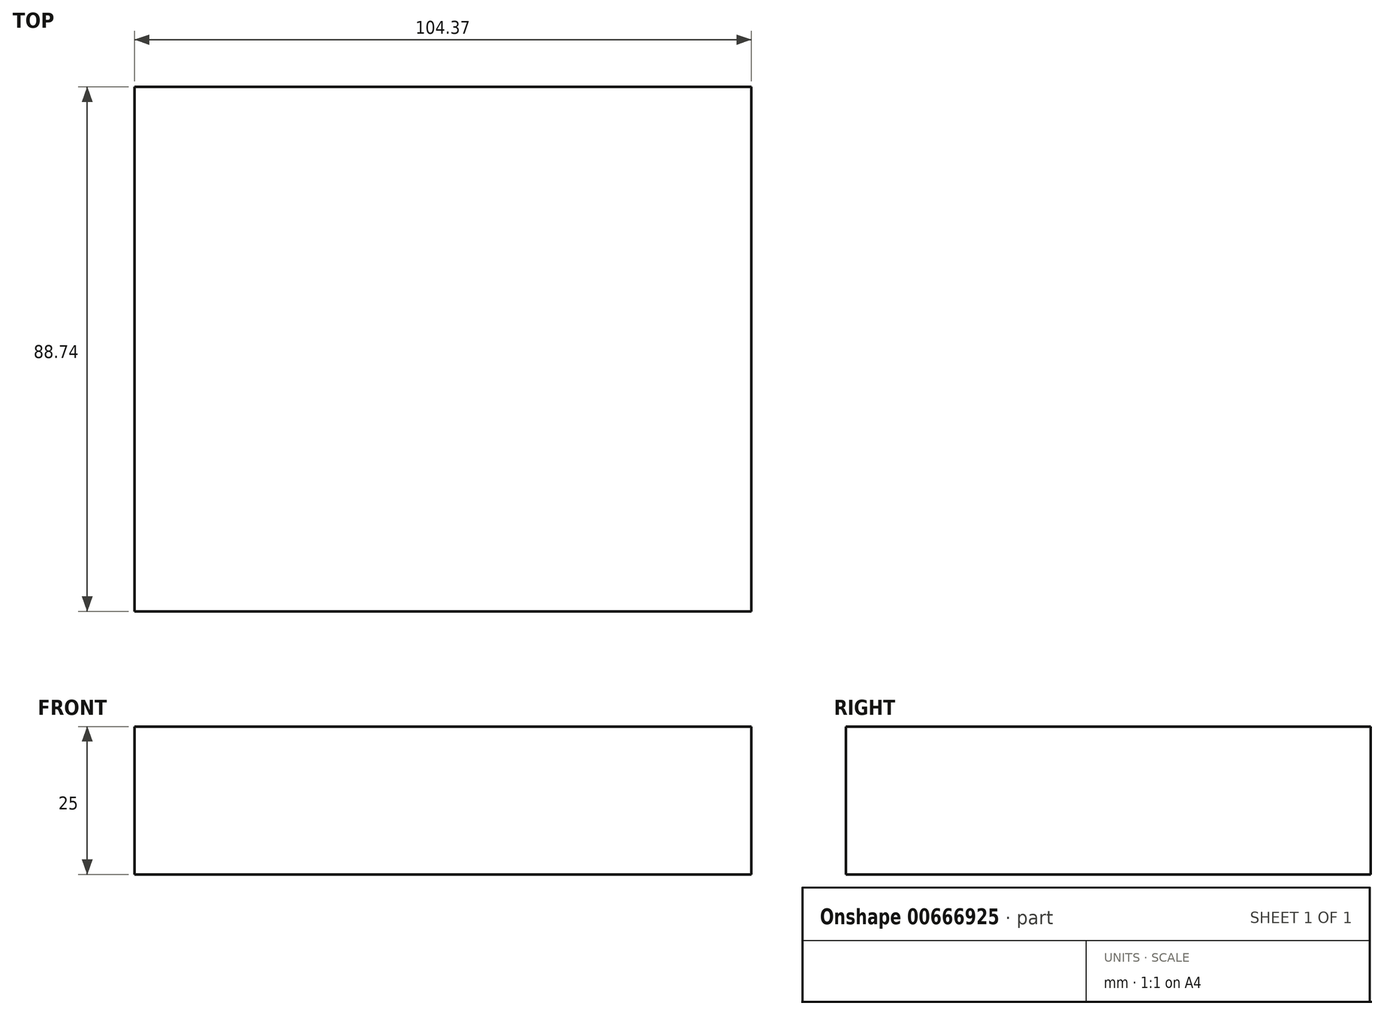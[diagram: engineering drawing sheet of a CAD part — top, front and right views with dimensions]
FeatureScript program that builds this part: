
annotation { "Feature Type Name" : "Feature", "Feature Type Description" : "" }
export const myFeature = defineFeature(function(context is Context, id is Id, definition is map)
    precondition{}
    {
        {
            var Q0;
            Q0=qCreatedBy(makeId("Top.planeOp"),FACE);
            var sketch = newSketch(context, id + "F0", { "sketchPlane" : qUnion([Q0])});
            skLineSegment(sketch, "E0.bottom", {"start": v(-23.27, 45.3) * mm, "end": v(81.1, 45.3) * mm});
            skLineSegment(sketch, "E0.top", {"start": v(-23.27, -43.43) * mm, "end": v(81.1, -43.43) * mm});
            skLineSegment(sketch, "E0.left", {"start": v(-23.27, 45.3) * mm, "end": v(-23.27, -43.43) * mm});
            skLineSegment(sketch, "E0.right", {"start": v(81.1, 45.3) * mm, "end": v(81.1, -43.43) * mm});
            skSolve(sketch);
        }
        {
            var Q0;
            Q0=makeQuery(id+"F0.imprint","IMPRINT",FACE,{"disambiguationData":[TD([[makeQuery(id+"F0.imprint","IMPRINT",EDGE,{"derivedFrom":sQuery(id+"F0.wireOp",EDGE,"E0.bottom")}),-1.0]])]});
            extrude(context, id + "F1", {"entities" : qUnion([Q0]), "depth" : 25 * mm, "offsetDistance" : 25 * mm});
        }
    });
